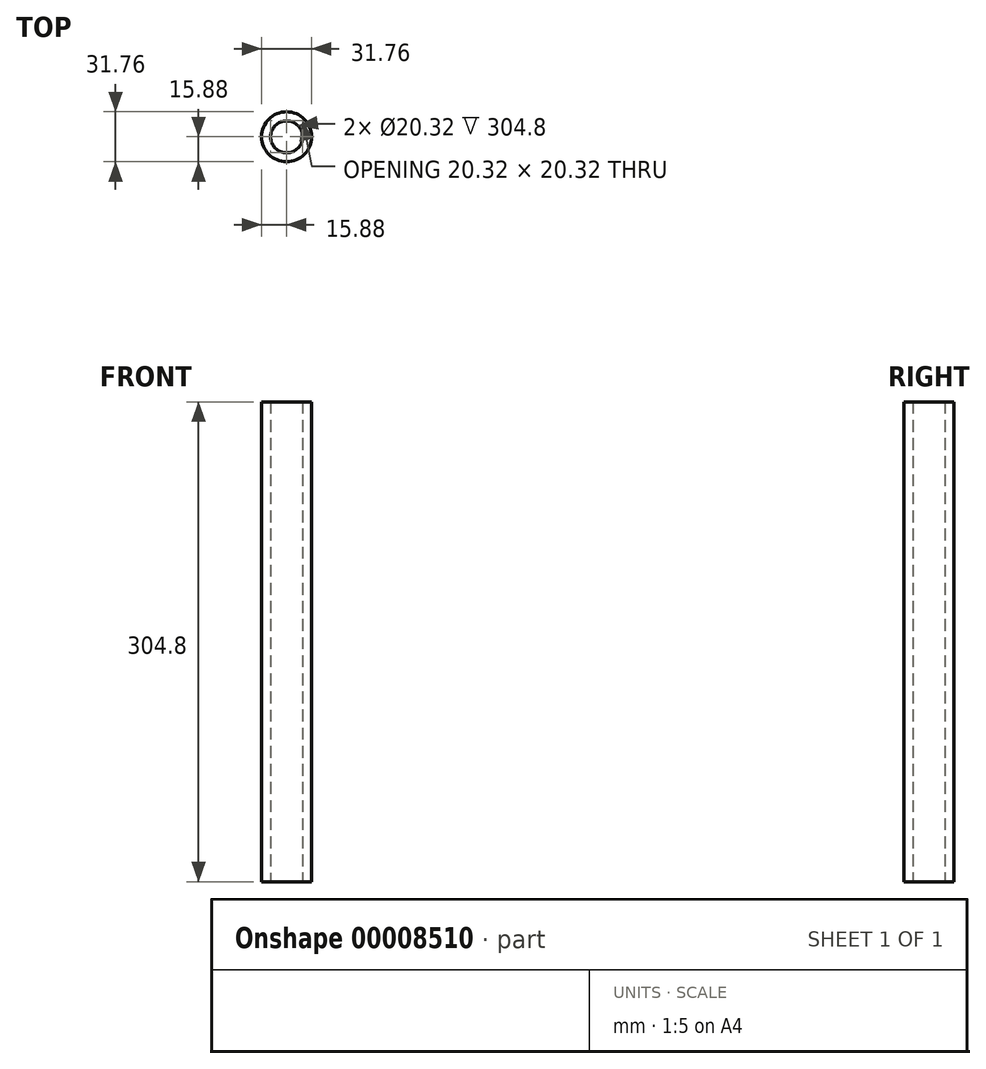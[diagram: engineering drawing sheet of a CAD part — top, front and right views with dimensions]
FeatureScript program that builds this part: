
annotation { "Feature Type Name" : "Feature", "Feature Type Description" : "" }
export const myFeature = defineFeature(function(context is Context, id is Id, definition is map)
    precondition{}
    {
        {
            var Q0;
            Q0=qCreatedBy(makeId("Top.planeOp"),FACE);
            var sketch = newSketch(context, id + "F0", { "sketchPlane" : qUnion([Q0])});
            skCircle(sketch, "E0", {"center": v(0, 0) * mm, "radius": 15.88 * mm});
            skSolve(sketch);
        }
        {
            var Q0;
            Q0=makeQuery(id+"F0.imprint","IMPRINT",FACE,{"disambiguationData":[TD([[makeQuery(id+"F0.imprint","IMPRINT",EDGE,{"derivedFrom":sQuery(id+"F0.wireOp",EDGE,"E0")}),1.0]])]});
            extrude(context, id + "F1", {"entities" : qUnion([Q0]), "depth" : 304.8 * mm});
        }
        {
            var Q0;
            Q0=makeQuery(id+"F1.opExtrude","CAP_FACE",FACE,{"disambiguationData":[OSD([sQuery(id+"F0.wireOp",EDGE,"E0")])],"isStart":true});
            var sketch = newSketch(context, id + "F2", { "sketchPlane" : qUnion([Q0])});
            skCircle(sketch, "E1", {"center": v(0, 0) * mm, "radius": 10.16 * mm});
            skSolve(sketch);
        }
        {
            var Q0;
            Q0=makeQuery(id+"F2.imprint","IMPRINT",FACE,{"disambiguationData":[TD([[makeQuery(id+"F2.imprint","IMPRINT",EDGE,{"derivedFrom":sQuery(id+"F2.wireOp",EDGE,"E1")}),1.0]])]});
            extrude(context, id + "F3", {"entities" : qUnion([Q0]), "operationType" : NewBodyOperationType.REMOVE, "oppositeDirection" : true, "depth" : 38.1 * mm});
        }
        {
            var Q0;
            Q0=makeQuery(id+"F1.opExtrude","CAP_FACE",FACE,{"disambiguationData":[OSD([sQuery(id+"F0.wireOp",EDGE,"E0")])],"isStart":false});
            var sketch = newSketch(context, id + "F4", { "sketchPlane" : qUnion([Q0])});
            skCircle(sketch, "E2", {"center": v(0, 0) * mm, "radius": 9.53 * mm});
            skSolve(sketch);
        }
        {
            var Q0;
            Q0=makeQuery(id+"F4.imprint","IMPRINT",FACE,{"disambiguationData":[TD([[makeQuery(id+"F4.imprint","IMPRINT",EDGE,{"derivedFrom":sQuery(id+"F4.wireOp",EDGE,"E2")}),1.0]])]});
            extrude(context, id + "F5", {"entities" : qUnion([Q0]), "operationType" : NewBodyOperationType.ADD, "depth" : 35.56 * mm});
        }
        {
            var Q0;
            Q0=makeQuery(id+"F3.boolean.opBoolean","COPY",FACE,{"derivedFrom":makeQuery(id+"F3.opExtrude","CAP_FACE",FACE,{"disambiguationData":[OSD([sQuery(id+"F2.wireOp",EDGE,"E1")])],"isStart":false})});
            extrude(context, id + "F6", {"entities" : qUnion([Q0]), "operationType" : NewBodyOperationType.REMOVE, "oppositeDirection" : true, "depth" : 508 * mm});
        }
    });
